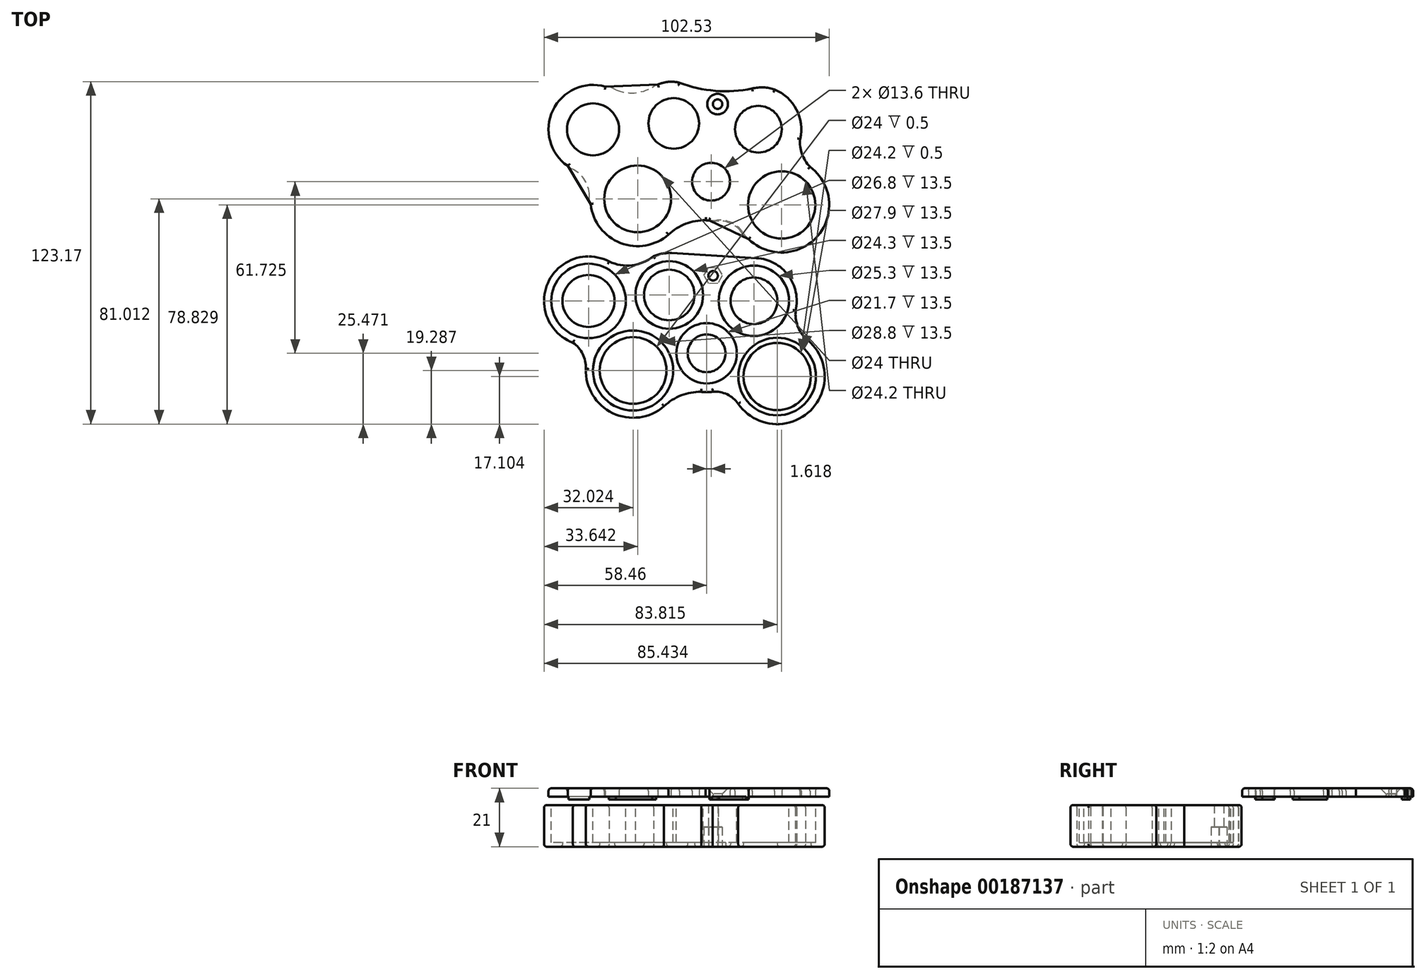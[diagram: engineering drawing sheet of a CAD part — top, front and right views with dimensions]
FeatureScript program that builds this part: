
annotation { "Feature Type Name" : "Feature", "Feature Type Description" : "" }
export const myFeature = defineFeature(function(context is Context, id is Id, definition is map)
    precondition{}
    {
        {
            var Q0;
            Q0=qCreatedBy(makeId("Top.planeOp"),FACE);
            var sketch = newSketch(context, id + "F0", { "sketchPlane" : qUnion([Q0])});
            skArc(sketch, "E0", {"start": v(-18.58, 19.68) * mm, "mid": v(-40.56, 11.98) * mm, "end": v(-31.57, -9.5) * mm});
            skArc(sketch, "E1", {"start": v(2.43, 22.7) * mm, "mid": v(-0.12, 22.37) * mm, "end": v(-2.57, 21.62) * mm});
            skArc(sketch, "E2", {"start": v(48.5, 2.02) * mm, "mid": v(45.84, 14.74) * mm, "end": v(34.4, 20.9) * mm});
            skArc(sketch, "E3", {"start": v(14.55, -27.21) * mm, "mid": v(16.64, -27.35) * mm, "end": v(18.72, -27.17) * mm});
            skArc(sketch, "E4", {"start": v(27.86, -31.53) * mm, "mid": v(53.8, -33.97) * mm, "end": v(52.05, -7.98) * mm});
            skArc(sketch, "E5", {"start": v(-26.9, -18.77) * mm, "mid": v(-17.33, -34.84) * mm, "end": v(1.21, -32.38) * mm});
            skCircle(sketch, "E6", {"center": v(-25.95, 5.48) * mm, "radius": 9.35 * mm});
            skCircle(sketch, "E7", {"center": v(-9.93, -19.53) * mm, "radius": 12 * mm});
            skCircle(sketch, "E8", {"center": v(3.07, 7.61) * mm, "radius": 9.1 * mm});
            skCircle(sketch, "E9", {"center": v(16.51, -13.35) * mm, "radius": 6.8 * mm});
            skCircle(sketch, "E10", {"center": v(33.5, 5.53) * mm, "radius": 8.4 * mm});
            skCircle(sketch, "E11", {"center": v(41.87, -21.72) * mm, "radius": 12.1 * mm});
            skPoint(sketch, "E12", {"position": v(17.46, 2.98) * mm});
            skPoint(sketch, "E13.orphan", {"position": v(18.29, 6.57) * mm});
            skPoint(sketch, "E14.orphan", {"position": v(25, -3.9) * mm});
            skPoint(sketch, "E15.trimOffspring.end.orphan", {"position": v(9.8, -2.87) * mm});
            skPoint(sketch, "E16.center.orphan", {"position": v(16.6, 25.02) * mm});
            skCircle(sketch, "E17", {"center": v(18.84, 14.55) * mm, "radius": 1.7 * mm});
            skArc(sketch, "E18", {"start": v(2.43, 22.7) * mm, "mid": v(3.2, 22.71) * mm, "end": v(3.96, 22.69) * mm});
            skCircle(sketch, "E19", {"center": v(33.5, 5.53) * mm, "radius": 12.5 * mm, "construction": true});
            skCircle(sketch, "E20", {"center": v(3.07, 7.61) * mm, "radius": 12.5 * mm, "construction": true});
            skLineSegment(sketch, "E21", {"start": v(3.07, 7.61) * mm, "end": v(33.5, 5.53) * mm, "construction": true});
            skLineSegment(sketch, "E22", {"start": v(18.29, 6.57) * mm, "end": v(20.04, 32.14) * mm, "construction": true});
            skArc(sketch, "E23", {"start": v(14.82, 17.04) * mm, "mid": v(16.36, 10.53) * mm, "end": v(22.86, 12.08) * mm, "construction": true});
            skLineSegment(sketch, "E24", {"start": v(3.96, 22.69) * mm, "end": v(34.4, 20.9) * mm});
            skArc(sketch, "E25", {"start": v(14.55, -27.21) * mm, "mid": v(7.38, -28.5) * mm, "end": v(1.21, -32.38) * mm});
            skCircle(sketch, "E26", {"center": v(-25.95, 5.48) * mm, "radius": 13.4 * mm, "construction": true});
            skCircle(sketch, "E27", {"center": v(-9.93, -19.53) * mm, "radius": 14.4 * mm, "construction": true});
            skCircle(sketch, "E28", {"center": v(16.51, -13.35) * mm, "radius": 10.85 * mm, "construction": true});
            skCircle(sketch, "E29", {"center": v(3.07, 7.61) * mm, "radius": 12.15 * mm, "construction": true});
            skCircle(sketch, "E30", {"center": v(33.5, 5.53) * mm, "radius": 12.65 * mm, "construction": true});
            skCircle(sketch, "E31", {"center": v(41.87, -21.72) * mm, "radius": 13.95 * mm, "construction": true});
            skArc(sketch, "E32", {"start": v(48.5, 2.02) * mm, "mid": v(49.19, -3.37) * mm, "end": v(52.05, -7.98) * mm});
            skArc(sketch, "E33", {"start": v(-18.58, 19.68) * mm, "mid": v(-12.6, 18.2) * mm, "end": v(-6.52, 19.28) * mm});
            skArc(sketch, "E34", {"start": v(-26.92, -18.94) * mm, "mid": v(-28.02, -13.62) * mm, "end": v(-31.57, -9.5) * mm});
            skArc(sketch, "E35", {"start": v(27.86, -31.53) * mm, "mid": v(23.88, -28.12) * mm, "end": v(18.72, -27.17) * mm});
            skArc(sketch, "E36", {"start": v(-6.52, 19.28) * mm, "mid": v(-4.46, 20.3) * mm, "end": v(-2.57, 21.62) * mm});
            skSolve(sketch);
        }
        {
            var Q0;
            Q0=makeQuery(id+"F0.imprint","IMPRINT",FACE,{"disambiguationData":[TD([[makeQuery(id+"F0.imprint","IMPRINT",EDGE,{"derivedFrom":sQuery(id+"F0.wireOp",EDGE,"E0")}),1.0]])]});
            extrude(context, id + "F1", {"entities" : qUnion([Q0]), "depth" : 15 * mm});
        }
        {
            var Q0;
            Q0=qCreatedBy(makeId("Top.planeOp"),FACE);
            cPlane(context, id + "F2", {"entities" : qUnion([Q0]), "cplaneType" : CPlaneType.OFFSET, "offset" : 18 * mm, "width" : 150 * mm, "height" : 150 * mm});
        }
        {
            var Q0;
            Q0=makeQuery(id+"F1.opExtrude","CAP_FACE",FACE,{"disambiguationData":[OSD([sQuery(id+"F0.wireOp",EDGE,"E0"),sQuery(id+"F0.wireOp",EDGE,"E1"),sQuery(id+"F0.wireOp",EDGE,"E2"),sQuery(id+"F0.wireOp",EDGE,"E3"),sQuery(id+"F0.wireOp",EDGE,"E4"),sQuery(id+"F0.wireOp",EDGE,"E5"),sQuery(id+"F0.wireOp",EDGE,"ujzqgH0S-dhHz-rYZF-uvIy-gRTnRsxaGosE"),sQuery(id+"F0.wireOp",EDGE,"7Unqwi8V-Efat-eiiR-riA2-7JwcXUSN4oi6"),sQuery(id+"F0.wireOp",EDGE,"Qgs0qyWt-UlJd-rMQj-xfdO-Boss06eYTIyV"),sQuery(id+"F0.wireOp",EDGE,"U8kQqLnC-B0kQ-Jbsu-NeVf-h4su2tbWtKO5"),sQuery(id+"F0.wireOp",EDGE,"y7Qm0ll6-VvSp-BIlt-Hxbv-nDPX4vQ1dLlo"),sQuery(id+"F0.wireOp",EDGE,"cmuSQvfR-1LlV-bjM8-RssA-lsbDypLqzE8I"),sQuery(id+"F0.wireOp",EDGE,"E16"),sQuery(id+"F0.wireOp",EDGE,"E6"),sQuery(id+"F0.wireOp",EDGE,"E7"),sQuery(id+"F0.wireOp",EDGE,"E8"),sQuery(id+"F0.wireOp",EDGE,"E9"),sQuery(id+"F0.wireOp",EDGE,"E10"),sQuery(id+"F0.wireOp",EDGE,"E11")])],"isStart":false});
            var sketch = newSketch(context, id + "F3", { "sketchPlane" : qUnion([Q0])});
            skCircle(sketch, "E37", {"center": v(-25.95, 5.48) * mm, "radius": 13.4 * mm});
            skCircle(sketch, "E38", {"center": v(-9.93, -19.53) * mm, "radius": 14.4 * mm});
            skCircle(sketch, "E39", {"center": v(16.51, -13.35) * mm, "radius": 10.85 * mm});
            skCircle(sketch, "E40", {"center": v(3.07, 7.61) * mm, "radius": 12.15 * mm});
            skCircle(sketch, "E41", {"center": v(33.5, 5.53) * mm, "radius": 12.65 * mm});
            skCircle(sketch, "E42", {"center": v(41.87, -21.72) * mm, "radius": 13.95 * mm});
            skSolve(sketch);
        }
        {
            var Q0;
            Q0=makeQuery(id+"F3.imprint","IMPRINT",FACE,{"disambiguationData":[TD([[makeQuery(id+"F3.imprint","IMPRINT",EDGE,{"derivedFrom":sQuery(id+"F3.wireOp",EDGE,"E37")}),1.0]])]});
            var Q1;
            Q1=makeQuery(id+"F3.imprint","IMPRINT",FACE,{"disambiguationData":[TD([[makeQuery(id+"F3.imprint","IMPRINT",EDGE,{"derivedFrom":sQuery(id+"F3.wireOp",EDGE,"E40")}),1.0]])]});
            var Q2;
            Q2=makeQuery(id+"F3.imprint","IMPRINT",FACE,{"disambiguationData":[TD([[makeQuery(id+"F3.imprint","IMPRINT",EDGE,{"derivedFrom":sQuery(id+"F3.wireOp",EDGE,"E41")}),1.0]])]});
            var Q3;
            Q3=makeQuery(id+"F3.imprint","IMPRINT",FACE,{"disambiguationData":[TD([[makeQuery(id+"F3.imprint","IMPRINT",EDGE,{"derivedFrom":sQuery(id+"F3.wireOp",EDGE,"E39")}),1.0]])]});
            var Q4;
            Q4=makeQuery(id+"F3.imprint","IMPRINT",FACE,{"disambiguationData":[TD([[makeQuery(id+"F3.imprint","IMPRINT",EDGE,{"derivedFrom":sQuery(id+"F3.wireOp",EDGE,"E38")}),1.0]])]});
            var Q5;
            Q5=makeQuery(id+"F3.imprint","IMPRINT",FACE,{"disambiguationData":[TD([[makeQuery(id+"F3.imprint","IMPRINT",EDGE,{"derivedFrom":sQuery(id+"F3.wireOp",EDGE,"E42")}),1.0]])]});
            extrude(context, id + "F4", {"entities" : qUnion([Q0, Q1, Q2, Q3, Q4, Q5]), "operationType" : NewBodyOperationType.REMOVE, "oppositeDirection" : true, "depth" : 13.5 * mm});
        }
        {
            var Q0;
            Q0=qCreatedBy(makeId("Top.planeOp"),FACE);
            var sketch = newSketch(context, id + "F5", { "sketchPlane" : qUnion([Q0])});
            skPoint(sketch, "E43", {"position": v(18.84, 14.62) * mm});
            skCircle(sketch, "E44.cCircle", {"center": v(18.84, 14.62) * mm, "radius": 2.86 * mm, "construction": true});
            skLineSegment(sketch, "E44.0", {"start": v(20.44, 17.5) * mm, "end": v(22.14, 14.67) * mm});
            skLineSegment(sketch, "E44.1", {"start": v(22.14, 14.67) * mm, "end": v(20.53, 11.8) * mm});
            skLineSegment(sketch, "E44.2", {"start": v(20.53, 11.8) * mm, "end": v(17.23, 11.74) * mm});
            skLineSegment(sketch, "E44.3", {"start": v(17.23, 11.74) * mm, "end": v(15.54, 14.57) * mm});
            skLineSegment(sketch, "E44.4", {"start": v(15.54, 14.57) * mm, "end": v(17.14, 17.45) * mm});
            skLineSegment(sketch, "E44.5", {"start": v(17.14, 17.45) * mm, "end": v(20.44, 17.5) * mm});
            skPoint(sketch, "E44.0.midPoint", {"position": v(21.29, 16.1) * mm});
            skPoint(sketch, "E45", {"position": v(18.84, 14.55) * mm});
            skSolve(sketch);
        }
        {
            var Q0;
            Q0=makeQuery(id+"F5.imprint","IMPRINT",FACE,{"disambiguationData":[TD([[makeQuery(id+"F5.imprint","IMPRINT",EDGE,{"derivedFrom":sQuery(id+"F5.wireOp",EDGE,"E44.0")}),-1.0]])]});
            extrude(context, id + "F6", {"entities" : qUnion([Q0]), "operationType" : NewBodyOperationType.REMOVE, "depth" : 7 * mm});
        }
        {
            var Q0;
            Q0=qCreatedBy(id+"F2.planeOp",FACE);
            var sketch = newSketch(context, id + "F7", { "sketchPlane" : qUnion([Q0])});
            skArc(sketch, "E46", {"start": v(-16.96, 81.4) * mm, "mid": v(-38.95, 73.7) * mm, "end": v(-29.95, 52.22) * mm});
            skArc(sketch, "E47", {"start": v(1.82, 84.16) * mm, "mid": v(0.41, 83.82) * mm, "end": v(-0.95, 83.34) * mm});
            skArc(sketch, "E48", {"start": v(50.12, 63.75) * mm, "mid": v(48.8, 74.32) * mm, "end": v(40.94, 81.51) * mm});
            skArc(sketch, "E49", {"start": v(16.17, 34.51) * mm, "mid": v(18.25, 34.38) * mm, "end": v(20.34, 34.55) * mm});
            skArc(sketch, "E50", {"start": v(29.48, 30.2) * mm, "mid": v(55.4, 27.75) * mm, "end": v(53.67, 53.74) * mm});
            skArc(sketch, "E51", {"start": v(-25.3, 42.95) * mm, "mid": v(-15.71, 26.89) * mm, "end": v(2.83, 29.35) * mm});
            skCircle(sketch, "E52", {"center": v(-24.33, 67.2) * mm, "radius": 9.35 * mm});
            skCircle(sketch, "E53", {"center": v(-8.3, 42.2) * mm, "radius": 12 * mm});
            skCircle(sketch, "E54", {"center": v(4.7, 69.34) * mm, "radius": 9.1 * mm});
            skCircle(sketch, "E55", {"center": v(18.13, 48.38) * mm, "radius": 6.8 * mm});
            skCircle(sketch, "E56", {"center": v(35.12, 67.25) * mm, "radius": 8.4 * mm});
            skCircle(sketch, "E57", {"center": v(43.48, 40) * mm, "radius": 12.1 * mm});
            skPoint(sketch, "E58", {"position": v(19.07, 64.7) * mm});
            skPoint(sketch, "E59.orphan", {"position": v(19.9, 68.3) * mm});
            skPoint(sketch, "E60.orphan", {"position": v(26.62, 57.81) * mm});
            skPoint(sketch, "E61.trimOffspring.end.orphan", {"position": v(11.41, 58.86) * mm});
            skPoint(sketch, "E62.center.orphan", {"position": v(18.21, 86.75) * mm});
            skCircle(sketch, "E63", {"center": v(20.45, 76.28) * mm, "radius": 1.7 * mm});
            skCircle(sketch, "E64", {"center": v(35.12, 67.25) * mm, "radius": 12.5 * mm, "construction": true});
            skCircle(sketch, "E65", {"center": v(4.7, 69.34) * mm, "radius": 12.5 * mm, "construction": true});
            skLineSegment(sketch, "E66", {"start": v(4.7, 69.34) * mm, "end": v(35.12, 67.25) * mm, "construction": true});
            skLineSegment(sketch, "E67", {"start": v(19.9, 68.3) * mm, "end": v(21.66, 93.87) * mm, "construction": true});
            skArc(sketch, "E68", {"start": v(16.17, 34.51) * mm, "mid": v(9, 33.23) * mm, "end": v(2.83, 29.35) * mm});
            skCircle(sketch, "E69", {"center": v(-24.33, 67.2) * mm, "radius": 13.4 * mm, "construction": true});
            skCircle(sketch, "E70", {"center": v(-8.3, 42.2) * mm, "radius": 14.4 * mm, "construction": true});
            skCircle(sketch, "E71", {"center": v(18.13, 48.38) * mm, "radius": 10.85 * mm, "construction": true});
            skCircle(sketch, "E72", {"center": v(4.7, 69.34) * mm, "radius": 12.15 * mm, "construction": true});
            skCircle(sketch, "E73", {"center": v(35.12, 67.25) * mm, "radius": 12.65 * mm, "construction": true});
            skCircle(sketch, "E74", {"center": v(43.48, 40) * mm, "radius": 13.95 * mm, "construction": true});
            skArc(sketch, "E75", {"start": v(50.12, 63.75) * mm, "mid": v(50.8, 58.36) * mm, "end": v(53.67, 53.74) * mm});
            skArc(sketch, "E76", {"start": v(-16.96, 81.4) * mm, "mid": v(-10.97, 79.93) * mm, "end": v(-4.9, 81) * mm});
            skArc(sketch, "E77", {"start": v(-25.3, 42.95) * mm, "mid": v(-26.44, 48.18) * mm, "end": v(-29.95, 52.22) * mm});
            skArc(sketch, "E78", {"start": v(29.48, 30.2) * mm, "mid": v(25.5, 33.6) * mm, "end": v(20.34, 34.55) * mm});
            skArc(sketch, "E79", {"start": v(21, 34.23) * mm, "mid": v(25.34, 33.3) * mm, "end": v(28.8, 30.52) * mm});
            skArc(sketch, "E80", {"start": v(-25.66, 43.53) * mm, "mid": v(-27.27, 48.9) * mm, "end": v(-31.41, 52.66) * mm});
            skArc(sketch, "E81", {"start": v(-16.16, 81.46) * mm, "mid": v(-9.48, 80.34) * mm, "end": v(-3.01, 82.36) * mm});
            skArc(sketch, "E82", {"start": v(-4.9, 81) * mm, "mid": v(-2.84, 82.02) * mm, "end": v(-0.95, 83.34) * mm});
            skArc(sketch, "E83.trimOffspring", {"start": v(23.85, 73) * mm, "mid": v(24.19, 73.39) * mm, "end": v(24.47, 73.8) * mm, "construction": true});
            skCircle(sketch, "E84", {"center": v(20.45, 76.28) * mm, "radius": 4.72 * mm, "construction": true});
            skArc(sketch, "E85", {"start": v(6.7, 83.97) * mm, "mid": v(19.63, 81.07) * mm, "end": v(32.86, 81.87) * mm});
            skArc(sketch, "E86", {"start": v(6.7, 83.97) * mm, "mid": v(4.28, 84.35) * mm, "end": v(1.82, 84.16) * mm});
            skArc(sketch, "E87", {"start": v(40.94, 81.51) * mm, "mid": v(36.93, 82.3) * mm, "end": v(32.86, 81.87) * mm});
            skLineSegment(sketch, "E88", {"start": v(-19.9, 82.58) * mm, "end": v(-0.95, 83.34) * mm});
            skLineSegment(sketch, "E89", {"start": v(-16.16, 81.46) * mm, "end": v(-18.66, 82.63) * mm});
            skLineSegment(sketch, "E90", {"start": v(-3.01, 82.36) * mm, "end": v(-1.6, 83.32) * mm});
            skLineSegment(sketch, "E91", {"start": v(17.5, 34.39) * mm, "end": v(31.67, 27.65) * mm});
            skLineSegment(sketch, "E92", {"start": v(31.67, 27.65) * mm, "end": v(30.75, 28.08) * mm});
            skLineSegment(sketch, "E93", {"start": v(30.75, 28.08) * mm, "end": v(28.8, 30.52) * mm});
            skLineSegment(sketch, "E94", {"start": v(21, 34.23) * mm, "end": v(18.44, 33.94) * mm});
            skLineSegment(sketch, "E95", {"start": v(-33.45, 54.05) * mm, "end": v(-25.2, 40.2) * mm});
            skLineSegment(sketch, "E96", {"start": v(-25.2, 40.2) * mm, "end": v(-25.71, 41.08) * mm});
            skLineSegment(sketch, "E97", {"start": v(-25.71, 41.08) * mm, "end": v(-25.66, 43.53) * mm});
            skLineSegment(sketch, "E98", {"start": v(-31.41, 52.66) * mm, "end": v(-33.14, 53.54) * mm});
            skSolve(sketch);
        }
        {
            var Q0;
            Q0=qSketchRegion(id+"F7",true);
            extrude(context, id + "F8", {"entities" : qUnion([Q0]), "depth" : 3 * mm});
        }
        {
            var Q0;
            Q0=makeQuery(id+"F1.opExtrude","CAP_EDGE",EDGE,{"disambiguationData":[OSD([sQuery(id+"F0.wireOp",EDGE,"E2")])],"isStart":true});
            var Q1;
            Q1=makeQuery(id+"F1.opExtrude","CAP_EDGE",EDGE,{"disambiguationData":[OSD([sQuery(id+"F0.wireOp",EDGE,"cmuSQvfR-1LlV-bjM8-RssA-lsbDypLqzE8I")])],"isStart":true});
            var Q2;
            Q2=makeQuery(id+"F1.opExtrude","CAP_EDGE",EDGE,{"disambiguationData":[OSD([sQuery(id+"F0.wireOp",EDGE,"E1")])],"isStart":true});
            var Q3;
            Q3=makeQuery(id+"F1.opExtrude","CAP_EDGE",EDGE,{"disambiguationData":[OSD([sQuery(id+"F0.wireOp",EDGE,"7Unqwi8V-Efat-eiiR-riA2-7JwcXUSN4oi6")])],"isStart":true});
            var Q4;
            Q4=makeQuery(id+"F1.opExtrude","CAP_EDGE",EDGE,{"disambiguationData":[OSD([sQuery(id+"F0.wireOp",EDGE,"E0")])],"isStart":true});
            var Q5;
            Q5=makeQuery(id+"F1.opExtrude","CAP_EDGE",EDGE,{"disambiguationData":[OSD([sQuery(id+"F0.wireOp",EDGE,"ujzqgH0S-dhHz-rYZF-uvIy-gRTnRsxaGosE")])],"isStart":true});
            var Q6;
            Q6=makeQuery(id+"F1.opExtrude","CAP_EDGE",EDGE,{"disambiguationData":[OSD([sQuery(id+"F0.wireOp",EDGE,"E5")])],"isStart":true});
            var Q7;
            Q7=makeQuery(id+"F1.opExtrude","CAP_EDGE",EDGE,{"disambiguationData":[OSD([sQuery(id+"F0.wireOp",EDGE,"y7Qm0ll6-VvSp-BIlt-Hxbv-nDPX4vQ1dLlo")])],"isStart":true});
            var Q8;
            Q8=makeQuery(id+"F1.opExtrude","CAP_EDGE",EDGE,{"disambiguationData":[OSD([sQuery(id+"F0.wireOp",EDGE,"E3")])],"isStart":true});
            var Q9;
            Q9=makeQuery(id+"F1.opExtrude","CAP_EDGE",EDGE,{"disambiguationData":[OSD([sQuery(id+"F0.wireOp",EDGE,"U8kQqLnC-B0kQ-Jbsu-NeVf-h4su2tbWtKO5")])],"isStart":true});
            var Q10;
            Q10=makeQuery(id+"F1.opExtrude","CAP_EDGE",EDGE,{"disambiguationData":[OSD([sQuery(id+"F0.wireOp",EDGE,"E4")])],"isStart":true});
            var Q11;
            Q11=makeQuery(id+"F1.opExtrude","CAP_EDGE",EDGE,{"disambiguationData":[OSD([sQuery(id+"F0.wireOp",EDGE,"Qgs0qyWt-UlJd-rMQj-xfdO-Boss06eYTIyV")])],"isStart":true});
            var Q12;
            Q12=makeQuery(id+"F1.opExtrude","CAP_EDGE",EDGE,{"disambiguationData":[OSD([sQuery(id+"F0.wireOp",EDGE,"E2")])],"isStart":false});
            var Q13;
            Q13=makeQuery(id+"F1.opExtrude","CAP_EDGE",EDGE,{"disambiguationData":[OSD([sQuery(id+"F0.wireOp",EDGE,"cmuSQvfR-1LlV-bjM8-RssA-lsbDypLqzE8I")])],"isStart":false});
            var Q14;
            Q14=makeQuery(id+"F1.opExtrude","CAP_EDGE",EDGE,{"disambiguationData":[OSD([sQuery(id+"F0.wireOp",EDGE,"E1")])],"isStart":false});
            var Q15;
            Q15=makeQuery(id+"F1.opExtrude","CAP_EDGE",EDGE,{"disambiguationData":[OSD([sQuery(id+"F0.wireOp",EDGE,"7Unqwi8V-Efat-eiiR-riA2-7JwcXUSN4oi6")])],"isStart":false});
            var Q16;
            Q16=makeQuery(id+"F1.opExtrude","CAP_EDGE",EDGE,{"disambiguationData":[OSD([sQuery(id+"F0.wireOp",EDGE,"E0")])],"isStart":false});
            var Q17;
            Q17=makeQuery(id+"F1.opExtrude","CAP_EDGE",EDGE,{"disambiguationData":[OSD([sQuery(id+"F0.wireOp",EDGE,"ujzqgH0S-dhHz-rYZF-uvIy-gRTnRsxaGosE")])],"isStart":false});
            var Q18;
            Q18=makeQuery(id+"F1.opExtrude","CAP_EDGE",EDGE,{"disambiguationData":[OSD([sQuery(id+"F0.wireOp",EDGE,"E5")])],"isStart":false});
            var Q19;
            Q19=makeQuery(id+"F1.opExtrude","CAP_EDGE",EDGE,{"disambiguationData":[OSD([sQuery(id+"F0.wireOp",EDGE,"y7Qm0ll6-VvSp-BIlt-Hxbv-nDPX4vQ1dLlo")])],"isStart":false});
            var Q20;
            Q20=makeQuery(id+"F1.opExtrude","CAP_EDGE",EDGE,{"disambiguationData":[OSD([sQuery(id+"F0.wireOp",EDGE,"E3")])],"isStart":false});
            var Q21;
            Q21=makeQuery(id+"F1.opExtrude","CAP_EDGE",EDGE,{"disambiguationData":[OSD([sQuery(id+"F0.wireOp",EDGE,"U8kQqLnC-B0kQ-Jbsu-NeVf-h4su2tbWtKO5")])],"isStart":false});
            var Q22;
            Q22=makeQuery(id+"F1.opExtrude","CAP_EDGE",EDGE,{"disambiguationData":[OSD([sQuery(id+"F0.wireOp",EDGE,"E4")])],"isStart":false});
            var Q23;
            Q23=makeQuery(id+"F1.opExtrude","CAP_EDGE",EDGE,{"disambiguationData":[OSD([sQuery(id+"F0.wireOp",EDGE,"Qgs0qyWt-UlJd-rMQj-xfdO-Boss06eYTIyV")])],"isStart":false});
            var Q24;
            Q24=makeQuery(id+"F1.opExtrude","CAP_EDGE",EDGE,{"disambiguationData":[OSD([sQuery(id+"F0.wireOp",EDGE,"RsfDVoeq-88MK-O4fM-M0ip-vEhRewOvGteJ")])],"isStart":true});
            var Q25;
            Q25=makeQuery(id+"F1.opExtrude","CAP_EDGE",EDGE,{"disambiguationData":[OSD([sQuery(id+"F0.wireOp",EDGE,"RsfDVoeq-88MK-O4fM-M0ip-vEhRewOvGteJ")])],"isStart":false});
            var Q26;
            Q26=makeQuery(id+"F1.opExtrude","CAP_EDGE",EDGE,{"disambiguationData":[OSD([sQuery(id+"F0.wireOp",EDGE,"cKg1eJ1H-dBtz-pCOY-6ZJL-w3ln1pFaWfeZ")])],"isStart":false});
            var Q27;
            Q27=makeQuery(id+"F1.opExtrude","CAP_EDGE",EDGE,{"disambiguationData":[OSD([sQuery(id+"F0.wireOp",EDGE,"cKg1eJ1H-dBtz-pCOY-6ZJL-w3ln1pFaWfeZ")])],"isStart":true});
            var Q28;
            Q28=makeQuery(id+"F1.opExtrude","CAP_EDGE",EDGE,{"disambiguationData":[OSD([sQuery(id+"F0.wireOp",EDGE,"E8")])],"isStart":true});
            var Q29;
            Q29=makeQuery(id+"F1.opExtrude","CAP_EDGE",EDGE,{"disambiguationData":[OSD([sQuery(id+"F0.wireOp",EDGE,"E10")])],"isStart":true});
            var Q30;
            Q30=makeQuery(id+"F1.opExtrude","CAP_EDGE",EDGE,{"disambiguationData":[OSD([sQuery(id+"F0.wireOp",EDGE,"E11")])],"isStart":true});
            var Q31;
            Q31=makeQuery(id+"F1.opExtrude","CAP_EDGE",EDGE,{"disambiguationData":[OSD([sQuery(id+"F0.wireOp",EDGE,"E9")])],"isStart":true});
            var Q32;
            Q32=makeQuery(id+"F1.opExtrude","CAP_EDGE",EDGE,{"disambiguationData":[OSD([sQuery(id+"F0.wireOp",EDGE,"E7")])],"isStart":true});
            var Q33;
            Q33=makeQuery(id+"F1.opExtrude","CAP_EDGE",EDGE,{"disambiguationData":[OSD([sQuery(id+"F0.wireOp",EDGE,"E6")])],"isStart":true});
            var Q34;
            Q34=makeQuery(id+"F1.opExtrude","CAP_EDGE",EDGE,{"disambiguationData":[OSD([sQuery(id+"F0.wireOp",EDGE,"E18")])],"isStart":false});
            var Q35;
            Q35=makeQuery(id+"F1.opExtrude","CAP_EDGE",EDGE,{"disambiguationData":[OSD([sQuery(id+"F0.wireOp",EDGE,"24nep5WU-dG8d-auV0-GWXn-9hRiig11i69S")])],"isStart":false});
            var Q36;
            Q36=makeQuery(id+"F1.opExtrude","CAP_EDGE",EDGE,{"disambiguationData":[OSD([sQuery(id+"F0.wireOp",EDGE,"ME7NNHAu-M7eQ-ST0F-Oq1P-V6rFcH8f88OT")])],"isStart":false});
            var Q37;
            Q37=makeQuery(id+"F1.opExtrude","CAP_EDGE",EDGE,{"disambiguationData":[OSD([sQuery(id+"F0.wireOp",EDGE,"E18")])],"isStart":true});
            var Q38;
            Q38=makeQuery(id+"F1.opExtrude","CAP_EDGE",EDGE,{"disambiguationData":[OSD([sQuery(id+"F0.wireOp",EDGE,"24nep5WU-dG8d-auV0-GWXn-9hRiig11i69S")])],"isStart":true});
            var Q39;
            Q39=makeQuery(id+"F1.opExtrude","CAP_EDGE",EDGE,{"disambiguationData":[OSD([sQuery(id+"F0.wireOp",EDGE,"ME7NNHAu-M7eQ-ST0F-Oq1P-V6rFcH8f88OT")])],"isStart":true});
            var Q40;
            Q40=makeQuery(id+"F1.opExtrude","CAP_EDGE",EDGE,{"disambiguationData":[OSD([sQuery(id+"F0.wireOp",EDGE,"E25")])],"isStart":false});
            var Q41;
            Q41=makeQuery(id+"F1.opExtrude","CAP_EDGE",EDGE,{"disambiguationData":[OSD([sQuery(id+"F0.wireOp",EDGE,"E35")])],"isStart":false});
            var Q42;
            Q42=makeQuery(id+"F1.opExtrude","CAP_EDGE",EDGE,{"disambiguationData":[OSD([sQuery(id+"F0.wireOp",EDGE,"E32")])],"isStart":false});
            var Q43;
            Q43=makeQuery(id+"F1.opExtrude","CAP_EDGE",EDGE,{"disambiguationData":[OSD([sQuery(id+"F0.wireOp",EDGE,"E34")])],"isStart":false});
            var Q44;
            Q44=makeQuery(id+"F1.opExtrude","CAP_EDGE",EDGE,{"disambiguationData":[OSD([sQuery(id+"F0.wireOp",EDGE,"E33"),sQuery(id+"F0.wireOp",EDGE,"E36")])],"isStart":false});
            var Q45;
            Q45=makeQuery(id+"F1.opExtrude","CAP_EDGE",EDGE,{"disambiguationData":[OSD([sQuery(id+"F0.wireOp",EDGE,"E24")])],"isStart":false});
            var Q46;
            Q46=makeQuery(id+"F1.opExtrude","CAP_EDGE",EDGE,{"disambiguationData":[OSD([sQuery(id+"F0.wireOp",EDGE,"E34")])],"isStart":true});
            var Q47;
            Q47=makeQuery(id+"F1.opExtrude","CAP_EDGE",EDGE,{"disambiguationData":[OSD([sQuery(id+"F0.wireOp",EDGE,"E25")])],"isStart":true});
            var Q48;
            Q48=makeQuery(id+"F1.opExtrude","CAP_EDGE",EDGE,{"disambiguationData":[OSD([sQuery(id+"F0.wireOp",EDGE,"E35")])],"isStart":true});
            var Q49;
            Q49=makeQuery(id+"F1.opExtrude","CAP_EDGE",EDGE,{"disambiguationData":[OSD([sQuery(id+"F0.wireOp",EDGE,"E33"),sQuery(id+"F0.wireOp",EDGE,"E36")])],"isStart":true});
            var Q50;
            Q50=makeQuery(id+"F1.opExtrude","CAP_EDGE",EDGE,{"disambiguationData":[OSD([sQuery(id+"F0.wireOp",EDGE,"E24")])],"isStart":true});
            var Q51;
            Q51=makeQuery(id+"F1.opExtrude","CAP_EDGE",EDGE,{"disambiguationData":[OSD([sQuery(id+"F0.wireOp",EDGE,"E32")])],"isStart":true});
            fillet(context, id + "F9", {"entities" : qUnion([Q0, Q1, Q2, Q3, Q4, Q5, Q6, Q7, Q8, Q9, Q10, Q11, Q12, Q13, Q14, Q15, Q16, Q17, Q18, Q19, Q20, Q21, Q22, Q23, Q24, Q25, Q26, Q27, Q28, Q29, Q30, Q31, Q32, Q33, Q34, Q35, Q36, Q37, Q38, Q39, Q40, Q41, Q42, Q43, Q44, Q45, Q46, Q47, Q48, Q49, Q50, Q51]), "radius" : 1 * mm, "tangentPropagation" : true, "allowEdgeOverflow" : false});
        }
        {
            var Q0;
            Q0=makeQuery(id+"F8.opExtrude","CAP_EDGE",EDGE,{"disambiguationData":[OSD([sQuery(id+"F7.wireOp",EDGE,"dd7925b3-5202-44ba-94b5-5ebd2e67dbee")])],"isStart":false});
            var Q1;
            Q1=makeQuery(id+"F8.opExtrude","CAP_EDGE",EDGE,{"disambiguationData":[OSD([sQuery(id+"F7.wireOp",EDGE,"E48")])],"isStart":false});
            var Q2;
            Q2=makeQuery(id+"F8.opExtrude","CAP_EDGE",EDGE,{"disambiguationData":[OSD([sQuery(id+"F7.wireOp",EDGE,"E75")])],"isStart":false});
            var Q3;
            Q3=makeQuery(id+"F8.opExtrude","CAP_EDGE",EDGE,{"disambiguationData":[OSD([sQuery(id+"F7.wireOp",EDGE,"E47"),sQuery(id+"F7.wireOp",EDGE,"59ef7708-9f98-4fb3-b6a6-863a0492b1ad")])],"isStart":false});
            var Q4;
            Q4=makeQuery(id+"F8.opExtrude","CAP_EDGE",EDGE,{"disambiguationData":[OSD([sQuery(id+"F7.wireOp",EDGE,"3q1dAgJg-svBi-AOCa-hUT2-8WAz32OXixbY")])],"isStart":false});
            var Q5;
            Q5=makeQuery(id+"F8.opExtrude","CAP_EDGE",EDGE,{"disambiguationData":[OSD([sQuery(id+"F7.wireOp",EDGE,"E46")])],"isStart":false});
            var Q6;
            Q6=makeQuery(id+"F8.opExtrude","CAP_EDGE",EDGE,{"disambiguationData":[OSD([sQuery(id+"F7.wireOp",EDGE,"rvuf3IW3-o8sk-oimQ-8lUD-dVfzTRyvGtw6")])],"isStart":false});
            var Q7;
            Q7=makeQuery(id+"F8.opExtrude","CAP_EDGE",EDGE,{"disambiguationData":[OSD([sQuery(id+"F7.wireOp",EDGE,"E51")])],"isStart":false});
            var Q8;
            Q8=makeQuery(id+"F8.opExtrude","CAP_EDGE",EDGE,{"disambiguationData":[OSD([sQuery(id+"F7.wireOp",EDGE,"E68")])],"isStart":false});
            var Q9;
            Q9=makeQuery(id+"F8.opExtrude","CAP_EDGE",EDGE,{"disambiguationData":[OSD([sQuery(id+"F7.wireOp",EDGE,"E49")])],"isStart":false});
            var Q10;
            Q10=makeQuery(id+"F8.opExtrude","CAP_EDGE",EDGE,{"disambiguationData":[OSD([sQuery(id+"F7.wireOp",EDGE,"tVISwAqm-pROy-ih1w-UG1K-MFPI976d3bC4")])],"isStart":false});
            var Q11;
            Q11=makeQuery(id+"F8.opExtrude","CAP_EDGE",EDGE,{"disambiguationData":[OSD([sQuery(id+"F7.wireOp",EDGE,"E52")])],"isStart":false});
            var Q12;
            Q12=makeQuery(id+"F8.opExtrude","CAP_EDGE",EDGE,{"disambiguationData":[OSD([sQuery(id+"F7.wireOp",EDGE,"E53")])],"isStart":false});
            var Q13;
            Q13=makeQuery(id+"F8.opExtrude","CAP_EDGE",EDGE,{"disambiguationData":[OSD([sQuery(id+"F7.wireOp",EDGE,"E54")])],"isStart":false});
            var Q14;
            Q14=makeQuery(id+"F8.opExtrude","CAP_EDGE",EDGE,{"disambiguationData":[OSD([sQuery(id+"F7.wireOp",EDGE,"E56")])],"isStart":false});
            var Q15;
            Q15=makeQuery(id+"F8.opExtrude","CAP_EDGE",EDGE,{"disambiguationData":[OSD([sQuery(id+"F7.wireOp",EDGE,"E55")])],"isStart":false});
            var Q16;
            Q16=makeQuery(id+"F8.opExtrude","CAP_EDGE",EDGE,{"disambiguationData":[OSD([sQuery(id+"F7.wireOp",EDGE,"E57")])],"isStart":false});
            var Q17;
            Q17=makeQuery(id+"F8.opExtrude","CAP_EDGE",EDGE,{"disambiguationData":[OSD([sQuery(id+"F7.wireOp",EDGE,"E86")])],"isStart":false});
            var Q18;
            Q18=makeQuery(id+"F8.opExtrude","CAP_EDGE",EDGE,{"disambiguationData":[OSD([sQuery(id+"F7.wireOp",EDGE,"E88")])],"isStart":false});
            var Q19;
            Q19=makeQuery(id+"F8.opExtrude","CAP_EDGE",EDGE,{"disambiguationData":[OSD([sQuery(id+"F7.wireOp",EDGE,"E85")])],"isStart":false});
            var Q20;
            Q20=makeQuery(id+"F8.opExtrude","CAP_EDGE",EDGE,{"disambiguationData":[OSD([sQuery(id+"F7.wireOp",EDGE,"E87")])],"isStart":false});
            var Q21;
            Q21=makeQuery(id+"F8.opExtrude","CAP_EDGE",EDGE,{"disambiguationData":[OSD([sQuery(id+"F7.wireOp",EDGE,"E50")])],"isStart":false});
            var Q22;
            Q22=makeQuery(id+"F8.opExtrude","CAP_EDGE",EDGE,{"disambiguationData":[OSD([sQuery(id+"F7.wireOp",EDGE,"E91"),sQuery(id+"F7.wireOp",EDGE,"E92")])],"isStart":false});
            var Q23;
            Q23=makeQuery(id+"F8.opExtrude","CAP_EDGE",EDGE,{"disambiguationData":[OSD([sQuery(id+"F7.wireOp",EDGE,"E95"),sQuery(id+"F7.wireOp",EDGE,"E96")])],"isStart":false});
            fillet(context, id + "F10", {"entities" : qUnion([Q0, Q1, Q2, Q3, Q4, Q5, Q6, Q7, Q8, Q9, Q10, Q11, Q12, Q13, Q14, Q15, Q16, Q17, Q18, Q19, Q20, Q21, Q22, Q23]), "radius" : 1 * mm, "tangentPropagation" : true, "allowEdgeOverflow" : false});
        }
        {
            var Q0;
            Q0=makeQuery(id+"F8.opExtrude","CAP_EDGE",EDGE,{"disambiguationData":[OSD([sQuery(id+"F7.wireOp",EDGE,"E63")])],"isStart":false});
            chamfer(context, id + "F11", {"entities" : qUnion([Q0]), "width" : 2 * mm, "tangentPropagation" : true});
        }
        {
            var Q0;
            {var subQ0=sQuery(id+"F7.wireOp",EDGE,"E79");Q0=makeQuery(id+"F7.imprint","IMPRINT",FACE,{"disambiguationData":[TD([[makeQuery(id+"F7.imprint","IMPRINT",EDGE,{"derivedFrom":subQ0}),-1.0]])]});}
            var Q1;
            {var subQ0=sQuery(id+"F7.wireOp",EDGE,"E81");Q1=makeQuery(id+"F7.imprint","IMPRINT",FACE,{"disambiguationData":[TD([[makeQuery(id+"F7.imprint","IMPRINT",EDGE,{"derivedFrom":subQ0}),1.0]])]});}
            var Q2;
            {var subQ0=sQuery(id+"F7.wireOp",EDGE,"E80");Q2=makeQuery(id+"F7.imprint","IMPRINT",FACE,{"disambiguationData":[TD([[makeQuery(id+"F7.imprint","IMPRINT",EDGE,{"derivedFrom":subQ0}),1.0]])]});}
            extrude(context, id + "F12", {"entities" : qUnion([Q0, Q1, Q2]), "operationType" : NewBodyOperationType.ADD, "oppositeDirection" : true, "depth" : 1 * mm});
        }
    });
